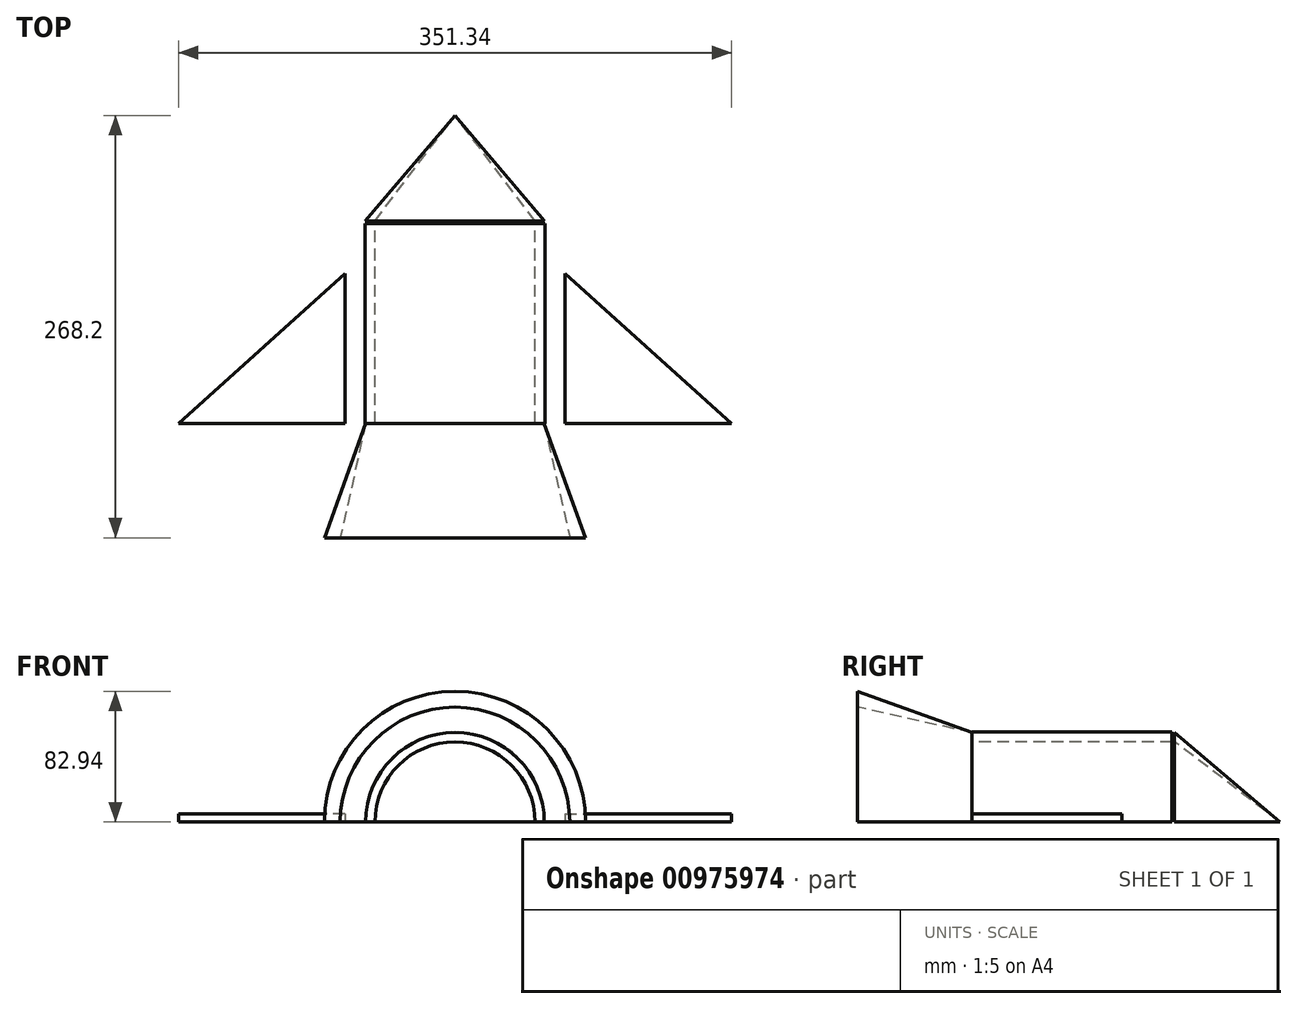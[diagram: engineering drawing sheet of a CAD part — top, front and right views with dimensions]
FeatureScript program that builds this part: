
annotation { "Feature Type Name" : "Feature", "Feature Type Description" : "" }
export const myFeature = defineFeature(function(context is Context, id is Id, definition is map)
    precondition{}
    {
        {
            var Q0;
            Q0=qCreatedBy(makeId("Top.planeOp"),FACE);
            var sketch = newSketch(context, id + "F0", { "sketchPlane" : qUnion([Q0])});
            skLineSegment(sketch, "E0", {"start": v(-50.8, 0) * mm, "end": v(-50.8, 127) * mm});
            skLineSegment(sketch, "E1", {"start": v(0, -4.07) * mm, "end": v(0, 27.63) * mm});
            skLineSegment(sketch, "E2", {"start": v(-50.8, 0) * mm, "end": v(-57.23, 0) * mm});
            skLineSegment(sketch, "E3", {"start": v(-57.23, 0) * mm, "end": v(-57.23, 127) * mm});
            skLineSegment(sketch, "E4", {"start": v(-50.8, 127) * mm, "end": v(-57.23, 127) * mm});
            skSolve(sketch);
        }
        {
            var Q0;
            Q0=makeQuery(id+"F0.imprint","IMPRINT",FACE,{"disambiguationData":[TD([[makeQuery(id+"F0.imprint","IMPRINT",EDGE,{"derivedFrom":sQuery(id+"F0.wireOp",EDGE,"E0")}),1.0]])]});
            var Q1;
            Q1=sQuery(id+"F0.wireOp",EDGE,"E1");
            revolve(context, id + "F1", {"surfaceOperationType" : NewSurfaceOperationType.NEW, "entities" : qUnion([Q0]), "axis" : qUnion([Q1]), "revolveType" : RevolveType.ONE_DIRECTION, "angle" : 180 * degree});
        }
        {
            var Q0;
            Q0=qCreatedBy(makeId("Top.planeOp"),FACE);
            var sketch = newSketch(context, id + "F2", { "sketchPlane" : qUnion([Q0])});
            skLineSegment(sketch, "E5", {"start": v(-69.8, 0) * mm, "end": v(-69.8, 95.08) * mm});
            skLineSegment(sketch, "E6", {"start": v(-69.8, 95.08) * mm, "end": v(-175.67, 0) * mm});
            skLineSegment(sketch, "E7", {"start": v(-69.8, 0) * mm, "end": v(-175.67, 0) * mm});
            skLineSegment(sketch, "E8.MirrorCS", {"start": v(69.8, 0) * mm, "end": v(69.8, 95.08) * mm});
            skLineSegment(sketch, "E9.MirrorCS", {"start": v(69.8, 0) * mm, "end": v(175.67, 0) * mm});
            skLineSegment(sketch, "E10.MirrorCS", {"start": v(69.8, 95.08) * mm, "end": v(175.67, 0) * mm});
            skSolve(sketch);
        }
        {
            var Q0;
            Q0=qCreatedBy(makeId("Top.planeOp"),FACE);
            var sketch = newSketch(context, id + "F3", { "sketchPlane" : qUnion([Q0])});
            skLineSegment(sketch, "E11", {"start": v(-56.99, 128.64) * mm, "end": v(0, 195.48) * mm});
            skLineSegment(sketch, "E12", {"start": v(0, 195.48) * mm, "end": v(0, 149.04) * mm});
            skLineSegment(sketch, "E13", {"start": v(-56.99, 128.64) * mm, "end": v(-50.92, 128.64) * mm});
            skLineSegment(sketch, "E14", {"start": v(-50.92, 128.64) * mm, "end": v(0, 195.48) * mm});
            skSolve(sketch);
        }
        {
            var Q0;
            Q0=makeQuery(id+"F3.imprint","IMPRINT",FACE,{"disambiguationData":[TD([[makeQuery(id+"F3.imprint","IMPRINT",EDGE,{"derivedFrom":sQuery(id+"F3.wireOp",EDGE,"E11")}),-1.0]])]});
            var Q1;
            Q1=sQuery(id+"F3.wireOp",EDGE,"E12");
            revolve(context, id + "F4", {"surfaceOperationType" : NewSurfaceOperationType.NEW, "entities" : qUnion([Q0]), "axis" : qUnion([Q1]), "revolveType" : RevolveType.ONE_DIRECTION, "oppositeDirection" : true, "angle" : 180 * degree});
        }
        {
            var Q0;
            Q0=qCreatedBy(makeId("Top.planeOp"),FACE);
            var sketch = newSketch(context, id + "F5", { "sketchPlane" : qUnion([Q0])});
            skLineSegment(sketch, "E15", {"start": v(-56.7, 0) * mm, "end": v(-82.94, -72.72) * mm});
            skLineSegment(sketch, "E16", {"start": v(-56.7, 0) * mm, "end": v(-72.9, -72.72) * mm});
            skLineSegment(sketch, "E17", {"start": v(0, 0) * mm, "end": v(0, -20.63) * mm});
            skLineSegment(sketch, "E18", {"start": v(-82.94, -72.72) * mm, "end": v(-72.9, -72.72) * mm});
            skSolve(sketch);
        }
        {
            var Q0;
            Q0=makeQuery(id+"F5.imprint","IMPRINT",FACE,{"disambiguationData":[TD([[makeQuery(id+"F5.imprint","IMPRINT",EDGE,{"derivedFrom":sQuery(id+"F5.wireOp",EDGE,"E15")}),1.0]])]});
            var Q1;
            Q1=sQuery(id+"F5.wireOp",EDGE,"E17");
            revolve(context, id + "F6", {"surfaceOperationType" : NewSurfaceOperationType.NEW, "entities" : qUnion([Q0]), "axis" : qUnion([Q1]), "revolveType" : RevolveType.ONE_DIRECTION, "oppositeDirection" : true, "angle" : 180 * degree});
        }
        {
            var Q0;
            Q0=makeQuery(id+"F2.imprint","IMPRINT",FACE,{"disambiguationData":[TD([[makeQuery(id+"F2.imprint","IMPRINT",EDGE,{"derivedFrom":sQuery(id+"F2.wireOp",EDGE,"E5")}),1.0]])]});
            var Q1;
            Q1=makeQuery(id+"F2.imprint","IMPRINT",FACE,{"disambiguationData":[TD([[makeQuery(id+"F2.imprint","IMPRINT",EDGE,{"derivedFrom":sQuery(id+"F2.wireOp",EDGE,"E8.MirrorCS")}),-1.0]])]});
            extrude(context, id + "F7", {"entities" : qUnion([Q0, Q1]), "depth" : 5.08 * mm, "offsetDistance" : 25.4 * mm});
        }
        {
            var Q0;
            Q0=qCreatedBy(makeId("Top.planeOp"),FACE);
            var sketch = newSketch(context, id + "F8", { "sketchPlane" : qUnion([Q0])});
            skPoint(sketch, "E19", {"position": v(0, -38.74) * mm});
            skLineSegment(sketch, "E20", {"start": v(0, -38.74) * mm, "end": v(0, -77.1) * mm});
            skLineSegment(sketch, "E21.bottom", {"start": v(-4.13, -77.92) * mm, "end": v(4.13, -77.92) * mm});
            skLineSegment(sketch, "E21.top", {"start": v(-4.13, -37.91) * mm, "end": v(4.13, -37.91) * mm});
            skLineSegment(sketch, "E21.left", {"start": v(-4.13, -77.92) * mm, "end": v(-4.13, -37.91) * mm});
            skLineSegment(sketch, "E21.right", {"start": v(4.13, -77.92) * mm, "end": v(4.13, -37.91) * mm});
            skPoint(sketch, "E21.middle", {"position": v(0, -57.92) * mm});
            skLineSegment(sketch, "E22", {"start": v(0, -77.1) * mm, "end": v(0, -77.92) * mm});
            skLineSegment(sketch, "E23", {"start": v(0, -38.74) * mm, "end": v(0, -37.91) * mm});
            skLineSegment(sketch, "E24", {"start": v(4.13, -77.92) * mm, "end": v(15.17, -77.92) * mm});
            skSolve(sketch);
        }
    });
